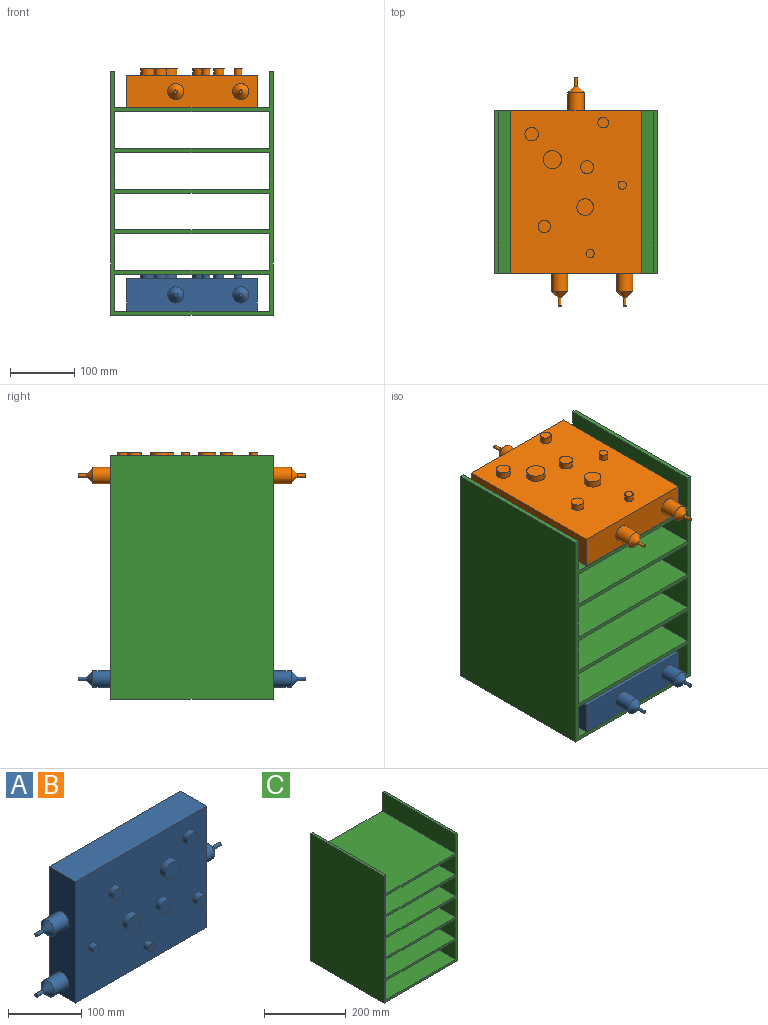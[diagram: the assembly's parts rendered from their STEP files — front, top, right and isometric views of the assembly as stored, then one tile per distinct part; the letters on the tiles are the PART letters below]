
ASSEMBLY  parts=3 mates=2
PART A: 34 faces, bbox 355.6x61x203.2 mm
  f0: plane 203.2x50.8mm, normal (-1,0,0), area 9309.1mm2, adj f1,f3,f4,f5,f23,f24
  f1: plane 254x203.2mm, normal (0,-1,0), area 49007.9mm2, adj f0,f2,f4,f5,f6,f8,f10,f12
  f2: plane 203.2x50.8mm, normal (1,0,0), area 9815.9mm2, adj f1,f3,f4,f5,f22
  f3: plane 254x203.2mm, normal (0,1,0), area 51612.8mm2, adj f0,f2,f4,f5
  f4: plane 254x50.8mm, normal (0,0,1), area 12903.2mm2, adj f0,f1,f2,f3
  f5: plane 254x50.8mm, normal (0,0,-1), area 12903.2mm2, adj f0,f1,f2,f3
  f6: cylinder r=9.63mm len=19.27mm, axis (0,1,0), area 615mm2, adj f1,f7
  f7: plane 19.27x19.27mm, normal (0,-1,0), area 291.6mm2, adj f6
  f8: cylinder r=14.2mm len=28.4mm, axis (0,1,0), area 906.4mm2, adj f1,f9
  f9: plane 28.4x28.4mm, normal (0,-1,0), area 633.3mm2, adj f8
  f10: cylinder r=12.97mm len=25.94mm, axis (0,1,0), area 828.1mm2, adj f1,f11
  f11: plane 25.94x25.94mm, normal (0,-1,0), area 528.6mm2, adj f10
  f12: cylinder r=8.37mm len=16.73mm, axis (0,1,0), area 534mm2, adj f1,f13
  f13: plane 16.73x16.73mm, normal (0,-1,0), area 219.8mm2, adj f12
  f14: cylinder r=6.44mm len=12.87mm, axis (0,1,0), area 410.9mm2, adj f1,f15
  f15: plane 12.87x12.87mm, normal (0,-1,0), area 130.2mm2, adj f14
  f16: cylinder r=6.41mm len=12.83mm, axis (0,1,0), area 409.4mm2, adj f1,f17
  f17: plane 12.83x12.83mm, normal (0,-1,0), area 129.2mm2, adj f16
  f18: cylinder r=10.12mm len=20.24mm, axis (0,1,0), area 646mm2, adj f1,f19
  f19: plane 20.24x20.24mm, normal (0,-1,0), area 321.7mm2, adj f18
  f20: cylinder r=10.56mm len=21.13mm, axis (0,1,0), area 674.3mm2, adj f1,f21
  f21: plane 21.13x21.13mm, normal (0,-1,0), area 350.5mm2, adj f20
  f22: cylinder r=12.7mm len=27.94mm, axis (-1,0,0), area 2229.5mm2, adj f2,f27
  f23: cylinder r=12.7mm len=27.94mm, axis (1,0,0), area 2229.5mm2, adj f0,f29
  f24: cylinder r=12.7mm len=27.94mm, axis (1,0,0), area 2229.5mm2, adj f0,f28
  f25: cylinder r=2.54mm len=12.7mm, axis (-1,0,0), area 202.7mm2, adj f26,f27
  f26: plane 5.08x5.08mm, normal (1,0,0), area 20.3mm2, adj f25
  f27: cone r=2.54mm half-angle=45deg, axis (-1,0,0), area 687.9mm2, adj f22,f25
  f28: cone r=2.54mm half-angle=45deg, axis (1,0,0), area 687.9mm2, adj f24,f32
  f29: cone r=2.54mm half-angle=45deg, axis (1,0,0), area 687.9mm2, adj f23,f30
  f30: cylinder r=2.54mm len=12.7mm, axis (1,0,0), area 202.7mm2, adj f29,f31
  f31: plane 5.08x5.08mm, normal (-1,0,0), area 20.3mm2, adj f30
  f32: cylinder r=2.54mm len=12.7mm, axis (1,0,0), area 202.7mm2, adj f28,f33
  f33: plane 5.08x5.08mm, normal (-1,0,0), area 20.3mm2, adj f32
PART B: same geometry as A
PART C: 30 faces, bbox 254x254x381 mm
  f0: plane 254x6.35mm, normal (0,0,1), area 1612.9mm2, adj f1,f2,f4,f29
  f1: plane 381x254mm, normal (0,-1,0), area 14032.2mm2, adj f0,f3,f4,f5,f6,f7,f8,f9
  f2: plane 381x254mm, normal (0,1,0), area 14032.2mm2, adj f0,f3,f4,f5,f6,f7,f8,f9
  f3: plane 381x254mm, normal (-1,0,0), area 96774mm2, adj f1,f2,f5,f6
  f4: plane 381x254mm, normal (1,0,0), area 96774mm2, adj f0,f1,f2,f6
  f5: plane 254x6.35mm, normal (0,0,1), area 1612.9mm2, adj f1,f2,f3,f27
  f6: plane 254x254mm, normal (0,0,-1), area 64516mm2, adj f1,f2,f3,f4
  f7: plane 254x241.3mm, normal (0,0,-1), area 61290.2mm2, adj f1,f2,f8,f9
  f8: plane 254x57.15mm, normal (-1,0,0), area 14516.1mm2, adj f1,f2,f7,f10
  f9: plane 254x57.15mm, normal (1,0,0), area 14516.1mm2, adj f1,f2,f7,f10
  f10: plane 254x241.3mm, normal (0,0,1), area 61290.2mm2, adj f1,f2,f8,f9
  f11: plane 254x241.3mm, normal (0,0,-1), area 61290.2mm2, adj f1,f2,f12,f13
  f12: plane 254x57.15mm, normal (-1,0,0), area 14516.1mm2, adj f1,f2,f11,f14
  f13: plane 254x57.15mm, normal (1,0,0), area 14516.1mm2, adj f1,f2,f11,f14
  f14: plane 254x241.3mm, normal (0,0,1), area 61290.2mm2, adj f1,f2,f12,f13
  f15: plane 254x241.3mm, normal (0,0,-1), area 61290.2mm2, adj f1,f2,f16,f17
  f16: plane 254x57.15mm, normal (-1,0,0), area 14516.1mm2, adj f1,f2,f15,f18
  f17: plane 254x57.15mm, normal (1,0,0), area 14516.1mm2, adj f1,f2,f15,f18
  f18: plane 254x241.3mm, normal (0,0,1), area 61290.2mm2, adj f1,f2,f16,f17
  f19: plane 254x241.3mm, normal (0,0,-1), area 61290.2mm2, adj f1,f2,f20,f21
  f20: plane 254x57.15mm, normal (-1,0,0), area 14516.1mm2, adj f1,f2,f19,f22
  f21: plane 254x57.15mm, normal (1,0,0), area 14516.1mm2, adj f1,f2,f19,f22
  f22: plane 254x241.3mm, normal (0,0,1), area 61290.2mm2, adj f1,f2,f20,f21
  f23: plane 254x241.3mm, normal (0,0,-1), area 61290.2mm2, adj f1,f2,f24,f25
  f24: plane 254x57.15mm, normal (-1,0,0), area 14516.1mm2, adj f1,f2,f23,f26
  f25: plane 254x57.15mm, normal (1,0,0), area 14516.1mm2, adj f1,f2,f23,f26
  f26: plane 254x241.3mm, normal (0,0,1), area 61290.2mm2, adj f1,f2,f24,f25
  f27: plane 254x57.15mm, normal (1,0,0), area 14516.1mm2, adj f1,f2,f5,f28
  f28: plane 254x241.3mm, normal (0,0,1), area 61290.2mm2, adj f1,f2,f27,f29
  f29: plane 254x57.15mm, normal (-1,0,0), area 14516.1mm2, adj f0,f1,f2,f28
PLACE A rot(axis=(-0.58,-0.58,0.58),120deg) t=(5.17,-33.03,17.22)mm
PLACE B rot(axis=(-0.58,-0.58,0.58),120deg) t=(5.17,-33.03,334.72)mm
PLACE C t=(-223.43,-33.03,-39.93)mm
MATE planar A.f3 <-> C.f10  axis (0,0,-1) through (-96.43,93.97,-33.58)mm
MATE planar B.f3 <-> C.f28  axis (0,0,-1) through (-96.43,93.97,283.92)mm
